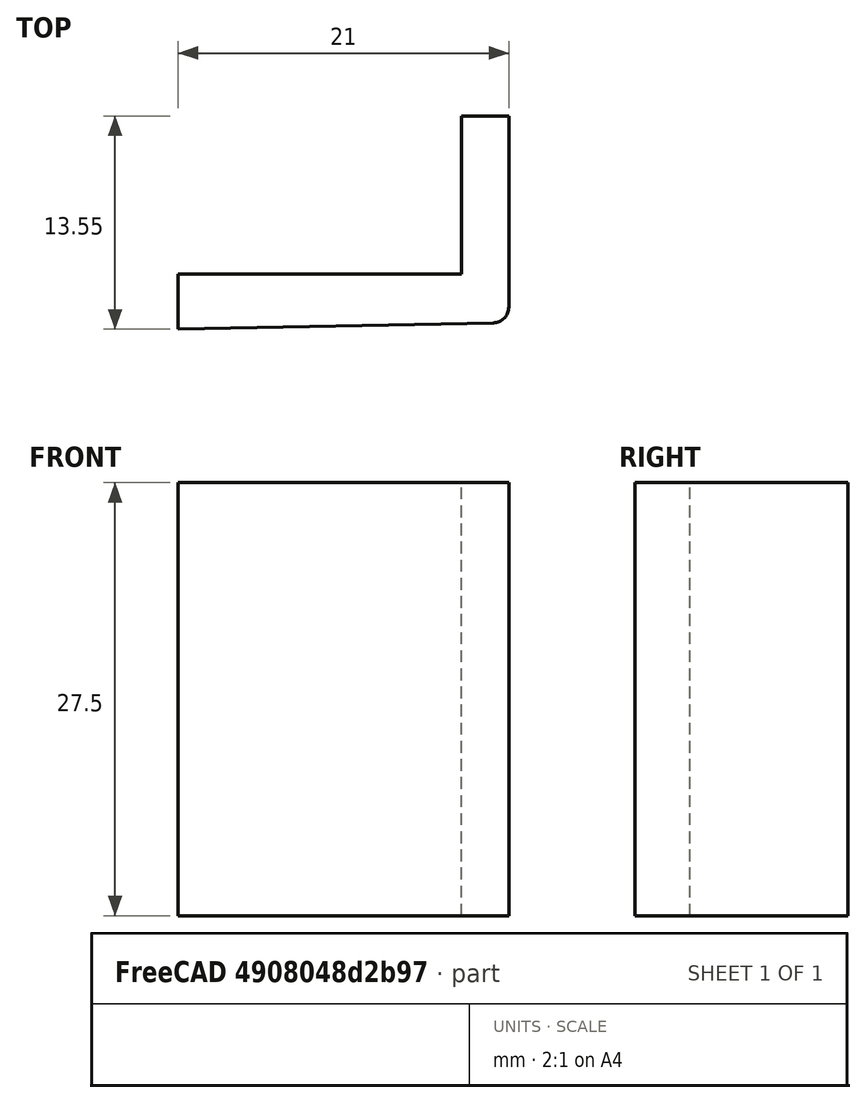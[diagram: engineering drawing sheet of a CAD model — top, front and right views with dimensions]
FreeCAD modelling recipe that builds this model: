
FCSTD DOCUMENT  (FreeCAD 0.19R24276 (Git))
Label: Outdoor-Screen-Handle
License: All rights reserved
LicenseURL: http://en.wikipedia.org/wiki/All_rights_reserved
objects: Sketcher::SketchObject×1, PartDesign::Pad×1, PartDesign::Body×1
note: 4 computed .brp shape members not serialized (recipe doc carries the construction recipe); baked Part::Feature solids carry a one-line shape summary decoded from their .brp

FEATURE [Sketcher::SketchObject] Sketch
  FullyConstrained = true
  MapMode = 5
  Support = -> [XY_Plane]
  sketch-geometry (7):
    g0: LineSegment StartX=0 StartY=0 StartZ=0 EndX=0 EndY=10.0498 EndZ=0
    g1: LineSegment StartX=0 StartY=10.0498 StartZ=0 EndX=3 EndY=10.0498 EndZ=0
    g2: LineSegment StartX=3 StartY=10.0498 StartZ=0 EndX=3 EndY=-2.1002 EndZ=0
    g3: LineSegment StartX=-18 StartY=-3.5 StartZ=0 EndX=-18 EndY=0 EndZ=0
    g4: LineSegment StartX=-18 StartY=0 StartZ=0 EndX=0 EndY=0 EndZ=0
    g5: LineSegment StartX=2.01998 StartY=-3.1 StartZ=0 EndX=-18 EndY=-3.5 EndZ=0
    g6: ArcOfCircle CenterX=2 CenterY=-2.1002 CenterZ=0 NormalX=0 NormalY=0 NormalZ=1 AngleXU=0 Radius=1 StartAngle=4.73237 EndAngle=6.28319
  constraints (19):
    c: Coincident(g-1,g0)
    c: PointOnObject(g0,g-2)
    c: Coincident(g0,g1)
    c: Horizontal(g1)
    c: Coincident(g1,g2)
    c: Vertical(g2)
    c: PointOnObject(g3,g-1)
    c: Vertical(g3)
    c: Coincident(g4,g3)
    c: Coincident(g4,g0)
    c: DistanceX(g1,g1) = 3
    c: DistanceX(g4,g4) = 18
    c: DistanceY(g3,g3) = 3.5
    c: Coincident(g5,g3)
    c: Tangent(g5,g6) = 1.5708
    c: Tangent(g2,g6) = 1.5708
    c: DistanceY(g2,g2) = 12.15
    c: Radius(g6) = 1
    c: DistanceY(g3,g5) = 0.4
FEATURE [PartDesign::Pad] Pad
  Direction = (1,1,1)
  Length = 27.5
  Length2 = 100
  Profile = -> Sketch
  Type = 0
FEATURE [PartDesign::Body] Body
  Group = -> [Sketch,Pad]
  Origin = -> Origin
  Tip = -> Pad
